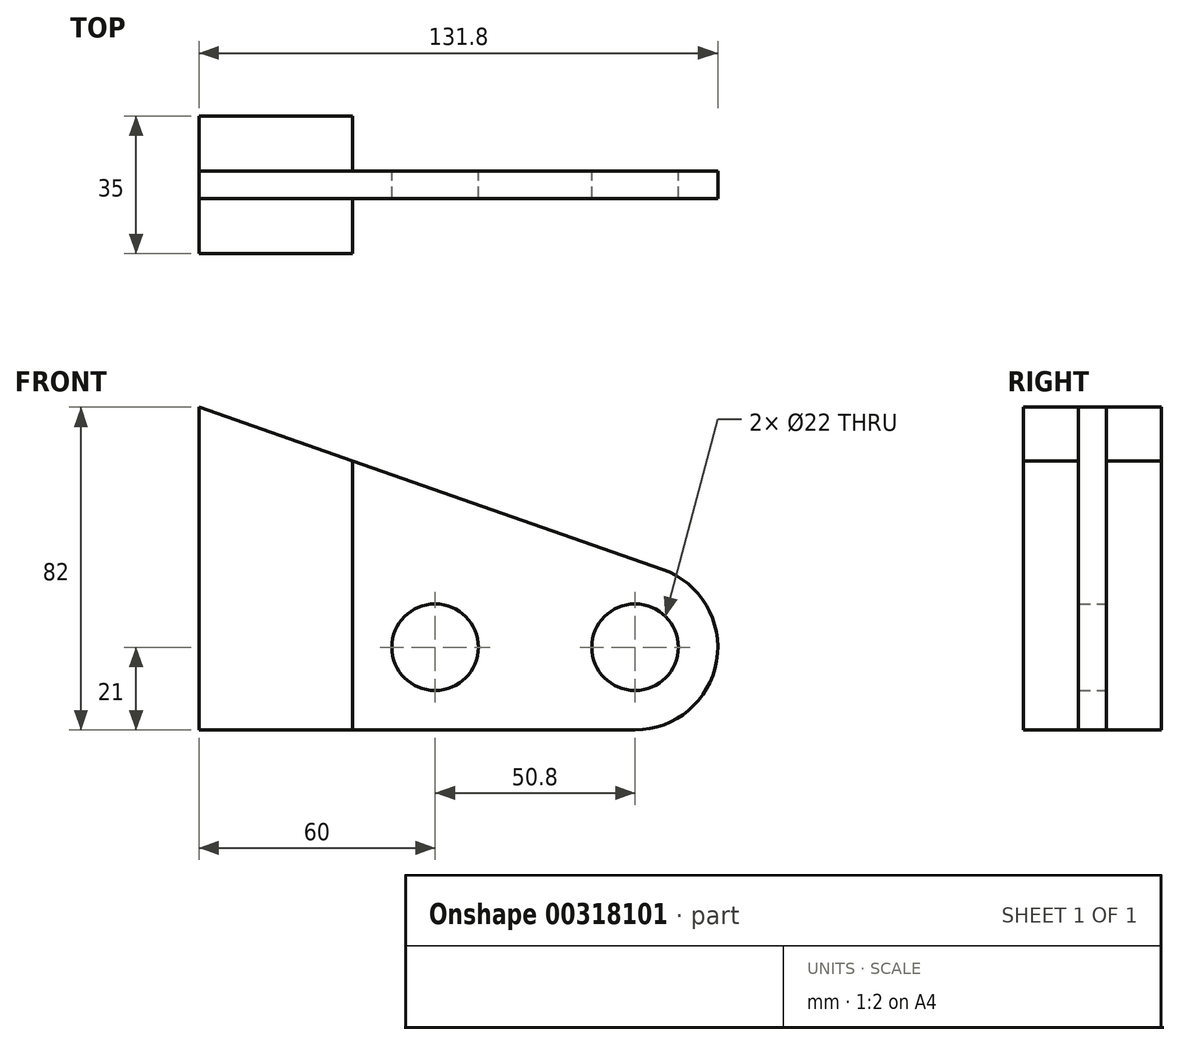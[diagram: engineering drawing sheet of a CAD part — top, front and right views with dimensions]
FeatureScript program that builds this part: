
annotation { "Feature Type Name" : "Feature", "Feature Type Description" : "" }
export const myFeature = defineFeature(function(context is Context, id is Id, definition is map)
    precondition{}
    {
        {
            var Q0;
            Q0=qCreatedBy(makeId("Front.planeOp"),FACE);
            var sketch = newSketch(context, id + "F0", { "sketchPlane" : qUnion([Q0])});
            skLineSegment(sketch, "E0", {"start": v(0, 0) * mm, "end": v(25.4, 0) * mm, "construction": true});
            skLineSegment(sketch, "E1", {"start": v(0, 0) * mm, "end": v(-25.4, 0) * mm, "construction": true});
            skCircle(sketch, "E2", {"center": v(-25.4, 0) * mm, "radius": 11 * mm});
            skCircle(sketch, "E3", {"center": v(25.4, 0) * mm, "radius": 11 * mm});
            skLineSegment(sketch, "E4", {"start": v(25.4, 21) * mm, "end": v(-85.4, 21) * mm});
            skLineSegment(sketch, "E5", {"start": v(25.4, -21) * mm, "end": v(-85.4, -21) * mm});
            skLineSegment(sketch, "E6", {"start": v(-85.4, 21) * mm, "end": v(-85.4, -21) * mm});
            skLineSegment(sketch, "E7", {"start": v(-85.4, 61) * mm, "end": v(-85.4, 21) * mm});
            skArc(sketch, "E8", {"start": v(25.4, -21) * mm, "mid": v(46.4, 0) * mm, "end": v(25.4, 21) * mm});
            skLineSegment(sketch, "E9", {"start": v(-85.4, 61) * mm, "end": v(32.33, 19.82) * mm});
            skSolve(sketch);
        }
        {
            var Q0;
            Q0=qSketchRegion(id+"F0",true);
            extrude(context, id + "F1", {"entities" : qUnion([Q0]), "endBound" : BoundingType.SYMMETRIC, "depth" : 7 * mm});
        }
        {
            var Q0;
            Q0=makeQuery(id+"F1.opExtrude","CAP_FACE",FACE,{"disambiguationData":[OSD([sQuery(id+"F0.wireOp",EDGE,"E2"),sQuery(id+"F0.wireOp",EDGE,"E3"),sQuery(id+"F0.wireOp",EDGE,"E5"),sQuery(id+"F0.wireOp",EDGE,"E6"),sQuery(id+"F0.wireOp",EDGE,"E7"),sQuery(id+"F0.wireOp",EDGE,"E8"),sQuery(id+"F0.wireOp",EDGE,"E9")])],"isStart":false});
            var sketch = newSketch(context, id + "F2", { "sketchPlane" : qUnion([Q0])});
            skCircle(sketch, "E10.0", {"center": v(-25.4, 0) * mm, "radius": 11 * mm});
            skLineSegment(sketch, "E10.1", {"start": v(-85.4, 61) * mm, "end": v(32.33, 19.82) * mm});
            skArc(sketch, "E10.2", {"start": v(25.4, -21) * mm, "mid": v(46.1, -3.52) * mm, "end": v(32.33, 19.82) * mm});
            skLineSegment(sketch, "E11.0", {"start": v(-85.4, 61) * mm, "end": v(-85.4, -21) * mm});
            skLineSegment(sketch, "E12.0", {"start": v(25.4, -21) * mm, "end": v(-85.4, -21) * mm});
            skLineSegment(sketch, "E13", {"start": v(-46.4, -21) * mm, "end": v(-46.4, 47.36) * mm});
            skSolve(sketch);
        }
        {
            var Q0;
            {var subQ0=sQuery(id+"F2.wireOp",EDGE,"E11.0");Q0=makeQuery(id+"F2.imprint","IMPRINT",FACE,{"disambiguationData":[TD([[makeQuery(id+"F2.imprint","IMPRINT",EDGE,{"derivedFrom":subQ0}),1.0]])]});}
            extrude(context, id + "F3", {"entities" : qUnion([Q0]), "depth" : 14 * mm});
        }
        {
            var Q0;
            Q0=makeQuery(id+"F3.opExtrude","SWEPT_BODY",BODY,{"disambiguationData":[OSD([sQuery(id+"F2.wireOp",EDGE,"E10.1"),sQuery(id+"F2.wireOp",EDGE,"E11.0"),sQuery(id+"F2.wireOp",EDGE,"E12.0"),sQuery(id+"F2.wireOp",EDGE,"E13")])]});
            var Q1;
            Q1=qCreatedBy(makeId("Front.planeOp"),FACE);
            mirror(context, id + "F4", {"entities" : qUnion([Q0]), "mirrorPlane" : qUnion([Q1])});
        }
    });
